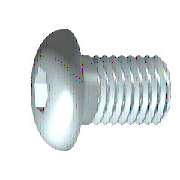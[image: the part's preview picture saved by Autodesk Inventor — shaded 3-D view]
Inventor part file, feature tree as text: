
AUTODESK INVENTOR PART (.ipt)
format: ipt  version: 2019 (Build 230136000, 136)  size: 199,680 bytes
history: native  units: mm (DEFAULTED — no unit token found)
features: sketch x2, extrude x1, plane x1, fillet x1
ambient origin geometry x7: Origin, YZ Plane, XY Plane, X Axis, Y Axis, Z Axis, Center Point
bodies: Solid1 (feature_tree), Body (feature_tree)
feature tree (5):
  extrude  "Slot"  Depth=1.65mm
  plane  "Work Plane1"
  fillet  "Fillet2"  Radius=1.65mm
  sketch  "Sketch1"  dims[d1=6.5mm d2=0.306825mm d3=1.65mm]
  sketch  "Sketch2"  dims[d4=1.04mm d5=60.0deg d6=3.0mm d7=3.0mm d8=2.309401mm d9=5.7mm d10=90.0deg d11=10.0mm d12=0.0mm d13=6.5mm d14=0.0mm d15=0.306725mm d16=0.306725mm d17=1.45mm d19=0.0mm d26=8.0mm d27=45.0deg d28=0.0mm d29=0.0mm d30=0.3mm]
